# Revit family: P210876JX-018_JED4536KB
name_source: partatom
category: Specialty Equipment
units: mm (PartAtom-declared; Revit-internal decimal feet)

## family parameters
Always vertical = Yes
Cut with Voids When Loaded = No
Enable Cutting in Views = No
Maintain Annotation Orientation = No
Part Type = Normal
Room Calculation Point = No
Round Connector Dimension = Use Diameter
Shared = No
Work Plane-Based = No

## types (1)
- JED4536KB
    Amps = 0 A
    Body Material = ARCAT - Metal - Steel - Stainless
    Cooktop Glass Material = ARCAT - Glass - Tempered - Black Light
    Default Elevation = 0"
    Depth = 22 1/16"
    Description = 36" Oblivion Glass Electric Radiant Downdraft Cooktop with Tap Touch Controls
Table de cuisson électrique radiante noire à évacuation descendante Jenn-Air® de 36 po
    Dimension Guide = https://access.whirlpool.com Guide&sku=JED4536GB&language=EN
https://access.whirlpool.com Guide&sku=JED4536GB&language=EN
    Family Name = Electric Downdraft Cooktop
    Feature 1 = JX3™ Downdraft Ventilation System with 3 Speeds
Ventilation à évacuation descendante JX3™ à 3 vitesses
    Feature 2 = Emotive Controls
Emotive Controls
    Feature 3 = Oblivion Glass Surface
Oblivion Glass Surface
    Height = 3 21/32"
    Installation-Fabrication = https://whirlpool.com
https://whirlpool.com
    Manufacturer = JennAir
    Model = JED4536KB
    Trim Material = ARCAT - Metal - Steel - Stainless Black
    Voltage = 0 V
    Width = 36 5/16"

## geometry (parser evidence)
native form markers: Sweep x4
no freeform markers — native parametric forms only
